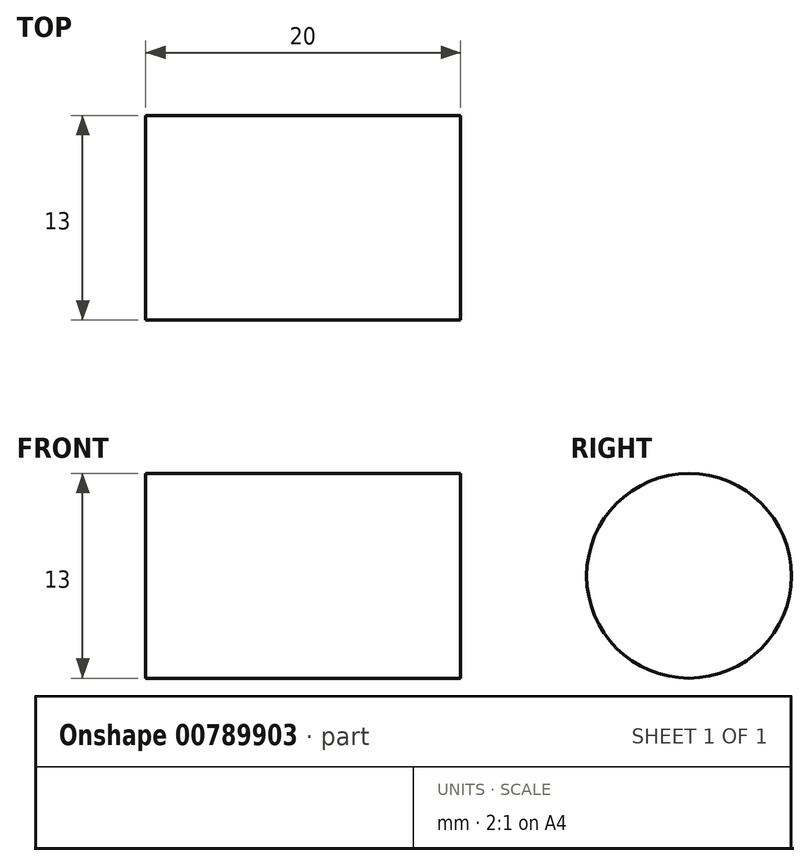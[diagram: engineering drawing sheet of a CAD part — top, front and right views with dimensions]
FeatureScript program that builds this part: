
annotation { "Feature Type Name" : "Feature", "Feature Type Description" : "" }
export const myFeature = defineFeature(function(context is Context, id is Id, definition is map)
    precondition{}
    {
        {
            var Q0;
            Q0=qCreatedBy(makeId("Right.planeOp"),FACE);
            var sketch = newSketch(context, id + "F0", { "sketchPlane" : qUnion([Q0])});
            skLineSegment(sketch, "E0", {"start": v(235.89, 805.44) * mm, "end": v(235.89, 400.44) * mm, "construction": true});
            skCircle(sketch, "E1", {"center": v(-302.16, -273.88) * mm, "radius": 50 * mm, "construction": true});
            skLineSegment(sketch, "E2", {"start": v(85.75, 157.25) * mm, "end": v(85.75, 169) * mm, "construction": true});
            skLineSegment(sketch, "E3", {"start": v(101.75, 157.25) * mm, "end": v(101.75, 169) * mm, "construction": true});
            skLineSegment(sketch, "E4", {"start": v(-254, -118.93) * mm, "end": v(-257.54, -122.46) * mm, "construction": true});
            skLineSegment(sketch, "E5", {"start": v(-296.43, -76.5) * mm, "end": v(-299.96, -80.04) * mm, "construction": true});
            skCircle(sketch, "E6", {"center": v(225, -180) * mm, "radius": 3.25 * mm, "construction": true});
            skCircle(sketch, "E7", {"center": v(110, 160) * mm, "radius": 6.5 * mm});
            skCircle(sketch, "E8", {"center": v(225, 185) * mm, "radius": 6.5 * mm});
            skCircle(sketch, "E9", {"center": v(225, -210) * mm, "radius": 6.5 * mm});
            skCircle(sketch, "E10", {"center": v(-100, -195) * mm, "radius": 10 * mm});
            skCircle(sketch, "E11", {"center": v(-325, 185) * mm, "radius": 6.5 * mm});
            skCircle(sketch, "E12", {"center": v(-295, 185) * mm, "radius": 11 * mm});
            skCircle(sketch, "E13", {"center": v(-346.17, -21.34) * mm, "radius": 2.12 * mm, "construction": true});
            skLineSegment(sketch, "E14", {"start": v(-346.17, -17.72) * mm, "end": v(-346.17, -24.97) * mm, "construction": true});
            skLineSegment(sketch, "E15", {"start": v(-349.8, -21.34) * mm, "end": v(-342.54, -21.34) * mm, "construction": true});
            skCircle(sketch, "E16", {"center": v(-242.2, -127.2) * mm, "radius": 2.12 * mm, "construction": true});
            skLineSegment(sketch, "E17", {"start": v(-242.2, -123.57) * mm, "end": v(-242.2, -130.82) * mm, "construction": true});
            skLineSegment(sketch, "E18", {"start": v(-245.82, -127.2) * mm, "end": v(-238.57, -127.2) * mm, "construction": true});
            skCircle(sketch, "E19", {"center": v(-136.34, -231.17) * mm, "radius": 2.12 * mm, "construction": true});
            skLineSegment(sketch, "E20", {"start": v(-136.34, -227.54) * mm, "end": v(-136.34, -234.8) * mm, "construction": true});
            skLineSegment(sketch, "E21", {"start": v(-139.97, -231.17) * mm, "end": v(-132.72, -231.17) * mm, "construction": true});
            skCircle(sketch, "E22", {"center": v(242.37, -227.37) * mm, "radius": 2.12 * mm, "construction": true});
            skLineSegment(sketch, "E23", {"start": v(242.37, -223.75) * mm, "end": v(242.37, -231) * mm, "construction": true});
            skLineSegment(sketch, "E24", {"start": v(238.75, -227.37) * mm, "end": v(246, -227.37) * mm, "construction": true});
            skCircle(sketch, "E25", {"center": v(247.5, -12.5) * mm, "radius": 2.12 * mm, "construction": true});
            skLineSegment(sketch, "E26", {"start": v(247.5, -8.88) * mm, "end": v(247.5, -16.13) * mm, "construction": true});
            skLineSegment(sketch, "E27", {"start": v(243.88, -12.5) * mm, "end": v(251.13, -12.5) * mm, "construction": true});
            skCircle(sketch, "E28", {"center": v(242.37, 202.37) * mm, "radius": 2.12 * mm, "construction": true});
            skLineSegment(sketch, "E29", {"start": v(242.37, 206) * mm, "end": v(242.37, 198.75) * mm, "construction": true});
            skLineSegment(sketch, "E30", {"start": v(238.75, 202.37) * mm, "end": v(246, 202.37) * mm, "construction": true});
            skCircle(sketch, "E31", {"center": v(47.37, 207.5) * mm, "radius": 2.12 * mm, "construction": true});
            skLineSegment(sketch, "E32", {"start": v(47.37, 211.12) * mm, "end": v(47.37, 203.87) * mm, "construction": true});
            skLineSegment(sketch, "E33", {"start": v(43.75, 207.5) * mm, "end": v(51, 207.5) * mm, "construction": true});
            skCircle(sketch, "E34", {"center": v(-147.37, 207.5) * mm, "radius": 2.12 * mm, "construction": true});
            skLineSegment(sketch, "E35", {"start": v(-147.37, 211.12) * mm, "end": v(-147.37, 203.87) * mm, "construction": true});
            skLineSegment(sketch, "E36", {"start": v(-151, 207.5) * mm, "end": v(-143.75, 207.5) * mm, "construction": true});
            skLineSegment(sketch, "E37", {"start": v(-346, 202.37) * mm, "end": v(-338.75, 202.37) * mm, "construction": true});
            skLineSegment(sketch, "E38", {"start": v(-342.37, 206) * mm, "end": v(-342.37, 198.75) * mm, "construction": true});
            skCircle(sketch, "E39", {"center": v(-342.37, 202.37) * mm, "radius": 2.12 * mm, "construction": true});
            skCircle(sketch, "E40", {"center": v(-252, 84) * mm, "radius": 20 * mm});
            skLineSegment(sketch, "E41", {"start": v(-125.84, -235) * mm, "end": v(83, -235) * mm, "construction": true});
            skLineSegment(sketch, "E42", {"start": v(-261, 210) * mm, "end": v(-330, 210) * mm, "construction": true});
            skLineSegment(sketch, "E43", {"start": v(250, -93.6) * mm, "end": v(250, -215) * mm, "construction": true});
            skLineSegment(sketch, "E44", {"start": v(250, 109.75) * mm, "end": v(250, -2.01) * mm, "construction": true});
            skLineSegment(sketch, "E45", {"start": v(-157.86, 210) * mm, "end": v(-261, 210) * mm, "construction": true});
            skLineSegment(sketch, "E46", {"start": v(36.89, 210) * mm, "end": v(-136.89, 210) * mm, "construction": true});
            skLineSegment(sketch, "E47", {"start": v(250, -22.99) * mm, "end": v(250, -93.6) * mm, "construction": true});
            skLineSegment(sketch, "E48", {"start": v(134, 210) * mm, "end": v(57.86, 210) * mm, "construction": true});
            skLineSegment(sketch, "E49", {"start": v(230, 210) * mm, "end": v(134, 210) * mm, "construction": true});
            skLineSegment(sketch, "E50", {"start": v(-146.45, -226.48) * mm, "end": v(-236.55, -136.38) * mm, "construction": true});
            skLineSegment(sketch, "E51", {"start": v(250, 190) * mm, "end": v(250, 109.75) * mm, "construction": true});
            skLineSegment(sketch, "E52", {"start": v(-147.32, -232.68) * mm, "end": v(-347.68, -32.32) * mm, "construction": true});
            skLineSegment(sketch, "E53", {"start": v(-355, -14.64) * mm, "end": v(-355, 190) * mm, "construction": true});
            skCircle(sketch, "E54", {"center": v(145, -145) * mm, "radius": 25 * mm});
            skLineSegment(sketch, "E55", {"start": v(255, 190) * mm, "end": v(255, -215) * mm, "construction": true});
            skLineSegment(sketch, "E56", {"start": v(230, 215) * mm, "end": v(-330, 215) * mm, "construction": true});
            skLineSegment(sketch, "E57", {"start": v(15, -193) * mm, "end": v(15, -222) * mm, "construction": true});
            skLineSegment(sketch, "E58", {"start": v(-20, -190) * mm, "end": v(12, -190) * mm, "construction": true});
            skLineSegment(sketch, "E59", {"start": v(-55, -196) * mm, "end": v(-55, -222) * mm, "construction": true});
            skLineSegment(sketch, "E60", {"start": v(-128.84, -231.17) * mm, "end": v(-128.84, -232) * mm, "construction": true});
            skLineSegment(sketch, "E61", {"start": v(234.87, -227.37) * mm, "end": v(234.87, -232) * mm, "construction": true});
            skLineSegment(sketch, "E62", {"start": v(-129.64, -240) * mm, "end": v(230, -240) * mm, "construction": true});
            skLineSegment(sketch, "E63", {"start": v(-52.3, -225) * mm, "end": v(12, -225) * mm, "construction": true});
            skLineSegment(sketch, "E64", {"start": v(225, -52.3) * mm, "end": v(225, 12) * mm, "construction": true});
            skLineSegment(sketch, "E65", {"start": v(196, -55) * mm, "end": v(222, -55) * mm, "construction": true});
            skLineSegment(sketch, "E66", {"start": v(190, -20) * mm, "end": v(190, 12) * mm, "construction": true});
            skLineSegment(sketch, "E67", {"start": v(193, 15) * mm, "end": v(222, 15) * mm, "construction": true});
            skLineSegment(sketch, "E68", {"start": v(65.12, 80) * mm, "end": v(247, 80) * mm, "construction": true});
            skLineSegment(sketch, "E69", {"start": v(91.21, -50) * mm, "end": v(190.08, -50) * mm, "construction": true});
            skLineSegment(sketch, "E70", {"start": v(-50, -91.22) * mm, "end": v(-50, -190.08) * mm, "construction": true});
            skLineSegment(sketch, "E71", {"start": v(227.92, -50) * mm, "end": v(247, -50) * mm, "construction": true});
            skLineSegment(sketch, "E72", {"start": v(83, -235) * mm, "end": v(231.87, -235) * mm, "construction": true});
            skLineSegment(sketch, "E73", {"start": v(-50, -227.92) * mm, "end": v(-50, -232) * mm, "construction": true});
            skLineSegment(sketch, "E74", {"start": v(-20, -190) * mm, "end": v(-55, -196) * mm, "construction": true});
            skLineSegment(sketch, "E75", {"start": v(190, -20) * mm, "end": v(196, -55) * mm, "construction": true});
            skCircle(sketch, "E76", {"center": v(140, 160) * mm, "radius": 14 * mm});
            skLineSegment(sketch, "E77", {"start": v(80, 167) * mm, "end": v(80, 147) * mm, "construction": true});
            skLineSegment(sketch, "E78", {"start": v(120, 167) * mm, "end": v(120, 147) * mm, "construction": true});
            skLineSegment(sketch, "E79", {"start": v(82, 145) * mm, "end": v(118.42, 145) * mm, "construction": true});
            skLineSegment(sketch, "E80", {"start": v(118, 169) * mm, "end": v(82, 169) * mm, "construction": true});
            skCircle(sketch, "E81", {"center": v(0, 0) * mm, "radius": 102.5 * mm});
            skLineSegment(sketch, "E82", {"start": v(225, 12) * mm, "end": v(225, -28.79) * mm, "construction": true});
            skCircle(sketch, "E83", {"center": v(177, -160) * mm, "radius": 9 * mm});
            skLineSegment(sketch, "E84", {"start": v(255, 190) * mm, "end": v(255, -215) * mm});
            skLineSegment(sketch, "E85", {"start": v(255, -215) * mm, "end": v(230, -240) * mm});
            skLineSegment(sketch, "E86", {"start": v(-129.64, -240) * mm, "end": v(230, -240) * mm});
            skLineSegment(sketch, "E87", {"start": v(-129.64, -240) * mm, "end": v(-147.32, -232.68) * mm});
            skLineSegment(sketch, "E88", {"start": v(-147.32, -232.68) * mm, "end": v(-347.68, -32.32) * mm});
            skLineSegment(sketch, "E89", {"start": v(-347.68, -32.32) * mm, "end": v(-355, -14.64) * mm});
            skLineSegment(sketch, "E90", {"start": v(-355, -14.64) * mm, "end": v(-355, 190) * mm});
            skLineSegment(sketch, "E91", {"start": v(-355, 190) * mm, "end": v(-330, 215) * mm});
            skLineSegment(sketch, "E92", {"start": v(-330, 215) * mm, "end": v(230, 215) * mm});
            skLineSegment(sketch, "E93", {"start": v(230, 215) * mm, "end": v(255, 190) * mm});
            skLineSegment(sketch, "E94.MirrorCS", {"start": v(-151.83, 384.27) * mm, "end": v(-159.08, 384.27) * mm, "construction": true});
            skLineSegment(sketch, "E95.MirrorCS", {"start": v(-107.4, 756.23) * mm, "end": v(-122.22, 758.47) * mm, "construction": true});
            skLineSegment(sketch, "E96.MirrorCS", {"start": v(-155.46, 387.9) * mm, "end": v(-155.46, 380.65) * mm, "construction": true});
            skLineSegment(sketch, "E97.MirrorCS", {"start": v(226.88, 388.07) * mm, "end": v(219.63, 388.07) * mm, "construction": true});
            skCircle(sketch, "E98.MirrorC", {"center": v(-155.46, 384.27) * mm, "radius": 2.12 * mm, "construction": true});
            skLineSegment(sketch, "E99.MirrorCS", {"start": v(-121.5, 748.25) * mm, "end": v(-120, 758.14) * mm, "construction": true});
            skLineSegment(sketch, "E100.MirrorCS", {"start": v(223.26, 391.7) * mm, "end": v(223.26, 384.44) * mm, "construction": true});
            skCircle(sketch, "E101.MirrorC", {"center": v(-127.84, 771.46) * mm, "radius": 2.12 * mm, "construction": true});
            skLineSegment(sketch, "E102.MirrorCS", {"start": v(-19.74, 501.64) * mm, "end": v(-11.68, 489) * mm, "construction": true});
            skLineSegment(sketch, "E103.MirrorCS", {"start": v(-111.11, 746.68) * mm, "end": v(-109.62, 756.56) * mm, "construction": true});
            skLineSegment(sketch, "E104.MirrorCS", {"start": v(-140.78, 751.17) * mm, "end": v(-139.28, 761.06) * mm, "construction": true});
            skLineSegment(sketch, "E105.MirrorCS", {"start": v(-137.05, 760.72) * mm, "end": v(-151.88, 762.97) * mm, "construction": true});
            skLineSegment(sketch, "E106.MirrorCS", {"start": v(-147.96, 384.27) * mm, "end": v(-147.96, 383.44) * mm, "construction": true});
            skLineSegment(sketch, "E107.MirrorCS", {"start": v(-107.4, 756.23) * mm, "end": v(-100.5, 801.7) * mm, "construction": true});
            skLineSegment(sketch, "E108.MirrorCS", {"start": v(-162.86, 822.94) * mm, "end": v(-170.11, 822.94) * mm, "construction": true});
            skLineSegment(sketch, "E109.MirrorCS", {"start": v(6.03, 479.82) * mm, "end": v(-2.4, 474.45) * mm, "construction": true});
            skLineSegment(sketch, "E110.MirrorCS", {"start": v(-122.22, 758.47) * mm, "end": v(-115.33, 803.96) * mm, "construction": true});
            skCircle(sketch, "E111.MirrorC", {"center": v(223.26, 388.07) * mm, "radius": 2.12 * mm, "construction": true});
            skLineSegment(sketch, "E112.MirrorCS", {"start": v(226.88, 817.82) * mm, "end": v(219.63, 817.82) * mm, "construction": true});
            skLineSegment(sketch, "E113.MirrorCS", {"start": v(-152.89, 753) * mm, "end": v(-109.38, 746.42) * mm, "construction": true});
            skLineSegment(sketch, "E114.MirrorCS", {"start": v(215.76, 388.07) * mm, "end": v(215.76, 383.44) * mm, "construction": true});
            skLineSegment(sketch, "E115.MirrorCS", {"start": v(-3.61, 476.34) * mm, "end": v(4.45, 463.7) * mm, "construction": true});
            skLineSegment(sketch, "E116.MirrorCS", {"start": v(-151.16, 752.74) * mm, "end": v(-149.66, 762.63) * mm, "construction": true});
            skLineSegment(sketch, "E117.MirrorCS", {"start": v(11.67, 470.97) * mm, "end": v(3.24, 465.6) * mm, "construction": true});
            skCircle(sketch, "E118.MirrorC", {"center": v(-17.76, 476.22) * mm, "radius": 2.12 * mm, "construction": true});
            skLineSegment(sketch, "E119.MirrorCS", {"start": v(-4.46, 496.27) * mm, "end": v(-12.89, 490.89) * mm, "construction": true});
            skLineSegment(sketch, "E120.MirrorCS", {"start": v(-361.66, 594.1) * mm, "end": v(-368.9, 594.1) * mm, "construction": true});
            skLineSegment(sketch, "E121.MirrorCS", {"start": v(-10.1, 505.12) * mm, "end": v(-18.53, 499.74) * mm, "construction": true});
            skLineSegment(sketch, "E122.MirrorCS", {"start": v(12.62, 469.5) * mm, "end": v(-11.04, 506.6) * mm, "construction": true});
            skLineSegment(sketch, "E123.MirrorCS", {"start": v(-145, 808.45) * mm, "end": v(-130.16, 806.2) * mm, "construction": true});
            skLineSegment(sketch, "E124.MirrorCS", {"start": v(-257.69, 488.24) * mm, "end": v(-264.94, 488.24) * mm, "construction": true});
            skLineSegment(sketch, "E125.MirrorCS", {"start": v(228.39, 606.57) * mm, "end": v(228.39, 599.32) * mm, "construction": true});
            skLineSegment(sketch, "E126.MirrorCS", {"start": v(28.26, 826.57) * mm, "end": v(28.26, 819.32) * mm, "construction": true});
            skLineSegment(sketch, "E127.MirrorCS", {"start": v(-115.33, 803.96) * mm, "end": v(-100.5, 801.7) * mm, "construction": true});
            skLineSegment(sketch, "E128.MirrorCS", {"start": v(-19.74, 501.64) * mm, "end": v(-58.53, 476.9) * mm, "construction": true});
            skLineSegment(sketch, "E129.MirrorCS", {"start": v(-34.33, 438.97) * mm, "end": v(-42.4, 451.61) * mm, "construction": true});
            skCircle(sketch, "E130.MirrorC", {"center": v(228.39, 602.94) * mm, "radius": 2.12 * mm, "construction": true});
            skLineSegment(sketch, "E131.MirrorCS", {"start": v(232.01, 602.94) * mm, "end": v(224.76, 602.94) * mm, "construction": true});
            skLineSegment(sketch, "E132.MirrorCS", {"start": v(-357.86, 817.82) * mm, "end": v(-365.11, 817.82) * mm, "construction": true});
            skCircle(sketch, "E133.MirrorC", {"center": v(-166.49, 822.94) * mm, "radius": 2.12 * mm, "construction": true});
            skLineSegment(sketch, "E134.MirrorCS", {"start": v(-11.68, 489) * mm, "end": v(-50.46, 464.26) * mm, "construction": true});
            skCircle(sketch, "E135.MirrorC", {"center": v(-365.28, 594.1) * mm, "radius": 2.12 * mm, "construction": true});
            skLineSegment(sketch, "E136.MirrorCS", {"start": v(-105.97, 748.93) * mm, "end": v(-97.88, 802.32) * mm, "construction": true});
            skCircle(sketch, "E137.MirrorC", {"center": v(-123.35, 801.12) * mm, "radius": 2.12 * mm, "construction": true});
            skCircle(sketch, "E138.MirrorC", {"center": v(-43.06, 460.09) * mm, "radius": 2.12 * mm, "construction": true});
            skCircle(sketch, "E139.MirrorC", {"center": v(205.89, 800.44) * mm, "radius": 6.5 * mm, "construction": true});
            skLineSegment(sketch, "E140.MirrorCS", {"start": v(-365.28, 597.72) * mm, "end": v(-365.28, 590.47) * mm, "construction": true});
            skLineSegment(sketch, "E141.MirrorCS", {"start": v(-143.9, 812.33) * mm, "end": v(-100.4, 805.74) * mm, "construction": true});
            skLineSegment(sketch, "E142.MirrorCS", {"start": v(-166.49, 826.57) * mm, "end": v(-166.49, 819.32) * mm, "construction": true});
            skLineSegment(sketch, "E143.MirrorCS", {"start": v(-155.4, 756.42) * mm, "end": v(-147.32, 809.81) * mm, "construction": true});
            skLineSegment(sketch, "E144.MirrorCS", {"start": v(-151.88, 762.97) * mm, "end": v(-145, 808.45) * mm, "construction": true});
            skLineSegment(sketch, "E145.MirrorCS", {"start": v(-261.31, 491.87) * mm, "end": v(-261.31, 484.62) * mm, "construction": true});
            skCircle(sketch, "E146.MirrorC", {"center": v(223.26, 817.82) * mm, "radius": 2.12 * mm, "construction": true});
            skLineSegment(sketch, "E147.MirrorCS", {"start": v(-3.61, 476.34) * mm, "end": v(-42.4, 451.61) * mm, "construction": true});
            skCircle(sketch, "E148.MirrorC", {"center": v(-261.31, 488.24) * mm, "radius": 2.12 * mm, "construction": true});
            skCircle(sketch, "E149.MirrorC", {"center": v(-361.49, 817.82) * mm, "radius": 2.12 * mm, "construction": true});
            skLineSegment(sketch, "E150.MirrorCS", {"start": v(-137.05, 760.72) * mm, "end": v(-130.16, 806.2) * mm, "construction": true});
            skLineSegment(sketch, "E151.MirrorCS", {"start": v(223.26, 821.44) * mm, "end": v(223.26, 814.2) * mm, "construction": true});
            skLineSegment(sketch, "E152.MirrorCS", {"start": v(4.45, 463.7) * mm, "end": v(-34.33, 438.97) * mm, "construction": true});
            skLineSegment(sketch, "E153.MirrorCS", {"start": v(-15.18, 507.51) * mm, "end": v(-60.72, 478.48) * mm, "construction": true});
            skLineSegment(sketch, "E154.MirrorCS", {"start": v(31.88, 822.94) * mm, "end": v(24.63, 822.94) * mm, "construction": true});
            skLineSegment(sketch, "E155.MirrorCS", {"start": v(-361.49, 821.44) * mm, "end": v(-361.49, 814.2) * mm, "construction": true});
            skCircle(sketch, "E156.MirrorC", {"center": v(-344.11, 800.44) * mm, "radius": 6.5 * mm, "construction": true});
            skCircle(sketch, "E157.MirrorC", {"center": v(28.26, 822.94) * mm, "radius": 2.12 * mm, "construction": true});
            skLineSegment(sketch, "E158.MirrorCS", {"start": v(-50.46, 464.26) * mm, "end": v(-58.53, 476.9) * mm, "construction": true});
            skLineSegment(sketch, "E159.MirrorCS", {"start": v(-37.98, 437.24) * mm, "end": v(-61.63, 474.34) * mm, "construction": true});
            skLineSegment(sketch, "E160.MirrorCS", {"start": v(11.7, 465.35) * mm, "end": v(-33.83, 436.32) * mm, "construction": true});
            skCircle(sketch, "E161.MirrorC", {"center": v(205.89, 405.44) * mm, "radius": 6.5 * mm, "construction": true});
            skLineSegment(sketch, "E162.MirrorCS", {"start": v(100.79, 790.3) * mm, "end": v(100.79, 760.58) * mm, "construction": true});
            skCircle(sketch, "E163.MirrorC", {"center": v(90.89, 775.44) * mm, "radius": 4.5 * mm, "construction": true});
            skCircle(sketch, "E164.MirrorC", {"center": v(120.89, 775.44) * mm, "radius": 14 * mm, "construction": true});
            skCircle(sketch, "E165.MirrorC", {"center": v(-119.11, 420.44) * mm, "radius": 10 * mm, "construction": true});
            skCircle(sketch, "E166.MirrorC", {"center": v(-329.45, 641.1) * mm, "radius": 5.5 * mm, "construction": true});
            skCircle(sketch, "E167.MirrorC", {"center": v(-271.11, 616.94) * mm, "radius": 5.5 * mm, "construction": true});
            skCircle(sketch, "E168.MirrorC", {"center": v(-188.61, 699.44) * mm, "radius": 5.5 * mm, "construction": true});
            skCircle(sketch, "E169.MirrorC", {"center": v(-212.78, 641.1) * mm, "radius": 5.5 * mm, "construction": true});
            skCircle(sketch, "E170.MirrorC", {"center": v(-212.78, 757.78) * mm, "radius": 5.5 * mm, "construction": true});
            skCircle(sketch, "E171.MirrorC", {"center": v(-329.45, 757.78) * mm, "radius": 5.5 * mm, "construction": true});
            skCircle(sketch, "E172.MirrorC", {"center": v(-353.61, 699.44) * mm, "radius": 5.5 * mm, "construction": true});
            skCircle(sketch, "E173.MirrorC", {"center": v(-271.11, 781.94) * mm, "radius": 5.5 * mm, "construction": true});
            skCircle(sketch, "E174.MirrorC", {"center": v(-314.11, 800.44) * mm, "radius": 11 * mm, "construction": true});
            skLineSegment(sketch, "E175.MirrorCS", {"start": v(-270.5, 493.9) * mm, "end": v(-360.6, 583.99) * mm, "construction": true});
            skLineSegment(sketch, "E176.MirrorCS", {"start": v(114.89, 825.44) * mm, "end": v(38.75, 825.44) * mm, "construction": true});
            skLineSegment(sketch, "E177.MirrorCS", {"start": v(230.89, 592.45) * mm, "end": v(230.89, 521.85) * mm, "construction": true});
            skCircle(sketch, "E178.MirrorC", {"center": v(-19.11, 615.44) * mm, "radius": 102.5 * mm, "construction": true});
            skLineSegment(sketch, "E179.MirrorCS", {"start": v(17.77, 825.44) * mm, "end": v(-156, 825.44) * mm, "construction": true});
            skLineSegment(sketch, "E180.MirrorCS", {"start": v(-374.11, 600.8) * mm, "end": v(-374.11, 805.44) * mm, "construction": true});
            skLineSegment(sketch, "E181.MirrorCS", {"start": v(-176.98, 825.44) * mm, "end": v(-349.11, 825.44) * mm, "construction": true});
            skLineSegment(sketch, "E182.MirrorCS", {"start": v(-144.96, 380.44) * mm, "end": v(212.76, 380.44) * mm, "construction": true});
            skLineSegment(sketch, "E183.MirrorCS", {"start": v(230.89, 725.2) * mm, "end": v(230.89, 613.43) * mm, "construction": true});
            skLineSegment(sketch, "E184.MirrorCS", {"start": v(-166.44, 382.76) * mm, "end": v(-366.8, 583.12) * mm, "construction": true});
            skLineSegment(sketch, "E185.MirrorCS", {"start": v(-369.11, 674.82) * mm, "end": v(-369.11, 805.44) * mm, "construction": true});
            skLineSegment(sketch, "E186.MirrorCS", {"start": v(-148.76, 375.44) * mm, "end": v(210.89, 375.44) * mm, "construction": true});
            skLineSegment(sketch, "E187.MirrorCS", {"start": v(210.89, 830.44) * mm, "end": v(-349.11, 830.44) * mm, "construction": true});
            skLineSegment(sketch, "E188.MirrorCS", {"start": v(230.89, 805.44) * mm, "end": v(230.89, 725.2) * mm, "construction": true});
            skLineSegment(sketch, "E189.MirrorCS", {"start": v(230.89, 521.85) * mm, "end": v(230.89, 400.44) * mm, "construction": true});
            skLineSegment(sketch, "E190.MirrorCS", {"start": v(-369.11, 604.57) * mm, "end": v(-369.11, 674.82) * mm, "construction": true});
            skCircle(sketch, "E191.MirrorC", {"center": v(125.89, 470.44) * mm, "radius": 25 * mm, "construction": true});
            skLineSegment(sketch, "E192.MirrorCS", {"start": v(210.89, 825.44) * mm, "end": v(114.89, 825.44) * mm, "construction": true});
            skLineSegment(sketch, "E193.MirrorCS", {"start": v(-165.57, 388.96) * mm, "end": v(-255.66, 479.06) * mm, "construction": true});
            skCircle(sketch, "E194.MirrorC", {"center": v(-271.11, 699.44) * mm, "radius": 55 * mm, "construction": true});
            skCircle(sketch, "E195", {"center": v(-252, 84) * mm, "radius": 55 * mm});
            skCircle(sketch, "E196", {"center": v(-271.11, 699.44) * mm, "radius": 82.5 * mm, "construction": true});
            skCircle(sketch, "E197", {"center": v(-252, 84) * mm, "radius": 82.5 * mm, "construction": true});
            skCircle(sketch, "E198", {"center": v(-169.5, 84) * mm, "radius": 5.5 * mm});
            skCircle(sketch, "E199.1.0", {"center": v(-193.66, 142.34) * mm, "radius": 5.5 * mm});
            skCircle(sketch, "E199.2.0", {"center": v(-252, 166.5) * mm, "radius": 5.5 * mm});
            skCircle(sketch, "E199.3.0", {"center": v(-310.34, 142.34) * mm, "radius": 5.5 * mm});
            skCircle(sketch, "E199.4.0", {"center": v(-334.5, 84) * mm, "radius": 5.5 * mm});
            skCircle(sketch, "E199.5.0", {"center": v(-310.34, 25.66) * mm, "radius": 5.5 * mm});
            skCircle(sketch, "E199.6.0", {"center": v(-252, 1.5) * mm, "radius": 5.5 * mm});
            skCircle(sketch, "E199.7.0", {"center": v(-193.66, 25.66) * mm, "radius": 5.5 * mm});
            skSolve(sketch);
        }
        {
            var Q0;
            Q0=makeQuery(id+"F0.imprint","IMPRINT",FACE,{"disambiguationData":[TD([[makeQuery(id+"F0.imprint","IMPRINT",EDGE,{"derivedFrom":sQuery(id+"F0.wireOp",EDGE,"E7")}),1.0]])]});
            extrude(context, id + "F1", {"entities" : qUnion([Q0]), "depth" : 20 * mm, "offsetDistance" : 25 * mm});
        }
    });
